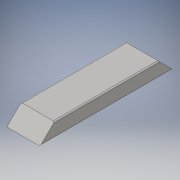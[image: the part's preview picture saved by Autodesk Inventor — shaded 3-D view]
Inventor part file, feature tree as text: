
AUTODESK INVENTOR PART (.ipt)
format: ipt  version: 2016 (Build 200138000, 138)  size: 99,840 bytes
history: native  units: in
note: dims shown in document units (in); Inventor stores cm internally (conversion verified against a paired STEP export)
features: extrude x1, chamfer x1, fillet x1, sketch x1
ambient origin geometry x8: Origin, YZ Plane, XZ Plane, XY Plane, X Axis, Y Axis, Z Axis, Center Point
bodies: Solid1 (feature_tree)
feature tree (4):
  extrude  "Extrusion1"  Depth=1.5in
  chamfer  "Chamfer1"  Distance=14.0in
  fillet  "Fillet1"  Radius=1.5in
  sketch  "Sketch1"  dims[d0=3.5in d1=1.5in d2=14.0in d3=0.0in d4=1.5in d5=0.125in d6=45.0deg d7=0.125in]
